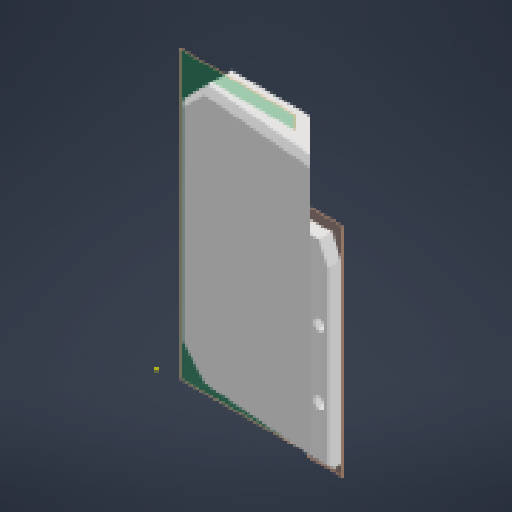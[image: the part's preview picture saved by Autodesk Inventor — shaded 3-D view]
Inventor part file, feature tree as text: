
AUTODESK INVENTOR PART (.ipt)
format: ipt  version: 2024 (Build 280153000, 153)  size: 1,187,328 bytes
history: native  units: in
note: dims shown in document units (in); Inventor stores cm internally (conversion verified against a paired STEP export)
features: sketch x21, reference x21, extrude x20, chamfer x13, projected_geometry x13, plane x8, other x5, fillet x1
ambient origin geometry x8: Origin, YZ Plane, XZ Plane, XY Plane, X Axis, Y Axis, Z Axis, Center Point
bodies: Solid1 (feature_tree)
feature tree (102):
  sketch  "Sketch1"  dims[d0=0.0157in d1=0.1181in]
  plane  "Work Plane1"
  extrude  "Extrusion1"  Depth=0.1181in
  sketch  "Sketch2"  dims[d2=1.0in d3=0.0in d4=0.7874in d6=0.2953in d7=2.3622in d9=0.2953in]
  plane  "Work Plane2"
  extrude  "Extrusion2"  Depth=0.7874in
  extrude  "Extrusion3"  Depth=3.1496in
  extrude  "Extrusion4"  Depth=0.1181in
  extrude  "Extrusion5"  Depth=0.1181in
  extrude  "Extrusion6"  Depth=1.0in TaperAngle=0.0deg
  chamfer  "Chamfer1"  Distance=0.0394in
  sketch  "Sketch7"  dims[d30=0.25in]
  plane  "Work Plane3"
  extrude  "Extrusion7"  Depth=0.0787in TaperAngle=0.0deg
  extrude  "Extrusion8"  Depth=0.125in TaperAngle=45.0deg
  chamfer  "Chamfer3"  Distance=0.4724in
  chamfer  "Chamfer5"  Distance=1.0in
  chamfer  "Chamfer7"  Distance=0.3912in Angle=15.0deg
  extrude  "Extrusion10"  Depth=0.0787in TaperAngle=15.0deg
  fillet  "Fillet2"  Radius=0.1181in
  chamfer  "Chamfer8"  Distance=0.42in Angle=15.0deg
  chamfer  "Chamfer9"  Distance=0.545in Angle=15.0deg
  chamfer  "Chamfer10"  Distance=0.0787in Angle=15.0deg
  chamfer  "Chamfer11"  Distance=2.1412in
  chamfer  "Chamfer12"  Distance=0.0787in
  chamfer  "Chamfer13"  Distance=0.2756in
  extrude  "Extrusion11"  Depth=0.1654in
  extrude  "Extrusion12"  Depth=0.1969in
  chamfer  "Chamfer14"  Distance=0.0787in
  extrude  "Extrusion13"  TaperAngle=45.0deg  [1 undecoded]
  chamfer  "Chamfer15"  Distance=1.0in
  chamfer  "Chamfer16"  Distance=0.1969in
  sketch  "Sketch14"  dims[d41=0.4724in d42=0.0in d43=0.125in d44=0.125in d45=45.0deg]
  plane  "Work Plane4"
  extrude  "Extrusion14"  Depth=0.1969in
  sketch  "Sketch15"  dims[d46=0.0118in]
  plane  "Work Plane5"
  extrude  "Extrusion15"  Depth=0.1969in TaperAngle=0.0deg
  plane  "Work Plane6"
  extrude  "Extrusion16"  Depth=0.1969in
  plane  "Work Plane7"
  sketch  "Sketch17"  dims[d53=0.2756in]
  plane  "Work Plane8"
  extrude  "Extrusion17"  Depth=0.1969in TaperAngle=0.0deg
  extrude  "Extrusion20"  TaperAngle=135.0deg  [1 undecoded]
  extrude  "Extrusion21"  Depth=0.1969in TaperAngle=0.0deg
  extrude  "Extrusion22"  [1 undecoded]
  extrude  "Extrusion23"  Depth=0.1969in
  reference  "Reference1"
  projected_geometry  "Projected Loop1"
  sketch  "Sketch3"  dims[d12=0.1952in d13=3.1496in d15=0.2953in d16=0.7874in d18=0.2953in]
  reference  "Reference2"
  reference  "Reference3"
  sketch  "Sketch4"  dims[d22=1.0in d23=0.0in d24=0.1181in]
  reference  "Reference4"
  reference  "Reference5"
  reference  "Reference6"
  reference  "Reference7"
  reference  "Reference8"
  reference  "Reference9"
  reference  "Reference10"
  sketch  "Sketch5"  dims[d25=0.1181in d26=0.1181in]
  projected_geometry  "Projected Loop2"
  sketch  "Sketch6"  dims[d27=0.1181in d28=1.0in d29=0.0in]
  projected_geometry  "Projected Loop3"
  projected_geometry  "Projected Loop4"
  reference  "Reference11"
  reference  "Reference12"
  reference  "Reference13"
  reference  "Reference14"
  reference  "Reference15"
  projected_geometry  "Projected Loop5"
  sketch  "Sketch8"  dims[d32=0.3937in]
  reference  "Reference16"
  reference  "Reference17"
  sketch  "Sketch10"  dims[d33=0.1181in]
  projected_geometry  "Projected Loop6"
  sketch  "Sketch11"  dims[d34=2.1654in]
  projected_geometry  "Projected Loop7"
  sketch  "Sketch12"  dims[d35=0.0984in d36=0.0394in d37=0.0in]
  projected_geometry  "Projected Loop8"
  sketch  "Sketch13"  dims[d38=0.1181in d39=0.0787in d40=0.0in]
  projected_geometry  "Projected Loop9"
  projected_geometry  "Projected Loop10"
  reference  "Reference19"
  reference  "Reference20"
  reference  "Reference21"
  reference  "Reference22"
  projected_geometry  "Projected Loop11"
  sketch  "Sketch16"  dims[d48=0.55in d49=0.4724in d50=0.0in d51=1.0in d52=0.0in]
  sketch  "Sketch18"  dims[d54=0.1575in d61=0.3912in d62=0.125in d63=15.0deg]
  sketch  "Sketch21"  dims[d67=0.8843in d68=0.125in d69=15.0deg d73=0.0787in d74=0.125in d75=15.0deg d76=0.1181in d77=0.0in]
  projected_geometry  "Projected Loop14"
  sketch  "Sketch22"  dims[d78=0.1181in d79=0.42in d80=0.125in d81=15.0deg d82=0.545in d83=0.125in d84=15.0deg d85=0.0787in d86=0.125in d87=15.0deg d88=2.1412in d89=0.125in d90=0.0344in d91=0.0787in d92=0.125in d93=0.0344in d94=0.2756in d95=0.125in d96=0.0344in]
  projected_geometry  "Projected Loop15"
  sketch  "Sketch24"  dims[d97=1.0in d98=0.0in d99=0.1654in]
  sketch  "Sketch25"  dims[d100=0.2756in d101=0.0in d102=0.0787in d103=0.125in d104=0.0344in d105=0.0787in d106=45.0deg d107=1.0in d108=0.0in d109=0.1969in d110=0.125in d111=0.0344in d112=0.0787in d113=0.125in d114=0.0344in d115=1.0in d116=0.0in d117=0.0118in d118=1.0in d119=0.0in d120=135.0deg d121=7.3125in d122=0.0in d123=-0.2953in d124=0.0079in d125=0.0079in d126=7.3125in d127=0.0in d132=3.9375in d133=0.0in d134=3.9375in d135=0.0in d136=3.9375in d137=0.0in d138=0.1654in d139=0.1654in d140=0.75in d141=1.0in d142=3.9375in d143=0.0in]
  other  "<userpath>\Desktop\SeniorDesign\Head_V3\Head_V3_Assembly.iam"
  other  "Head_V3_Assembly.iam"
  other  "Head_base_mount:1"
  other  "Assembly5"
  other  "Head_Left_Panel:1"
note: 3 required parameter values undecoded (feature->parameter linkage not recoverable at this tier; creation-order binding heuristic only, values carry confidence <= 0.55)
